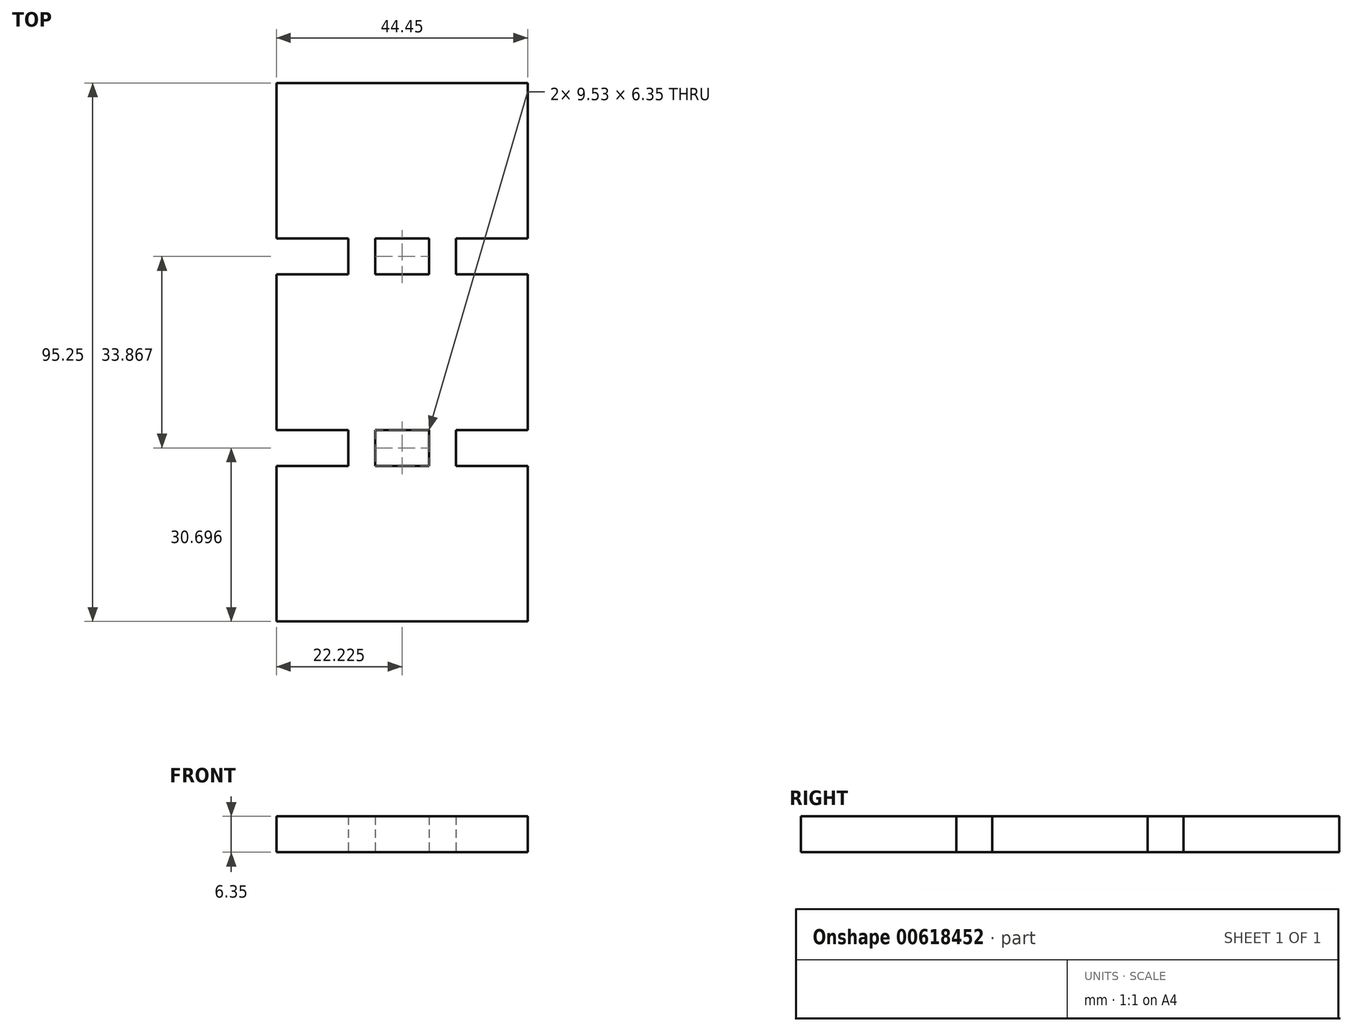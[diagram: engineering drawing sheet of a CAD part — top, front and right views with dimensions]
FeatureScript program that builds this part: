
annotation { "Feature Type Name" : "Feature", "Feature Type Description" : "" }
export const myFeature = defineFeature(function(context is Context, id is Id, definition is map)
    precondition{}
    {
        {
            var Q0;
            Q0=qCreatedBy(makeId("Top.planeOp"),FACE);
            var sketch = newSketch(context, id + "F0", { "sketchPlane" : qUnion([Q0])});
            skLineSegment(sketch, "E0.bottom", {"start": v(-25.4, -50.99) * mm, "end": v(19.05, -50.99) * mm});
            skLineSegment(sketch, "E0.top", {"start": v(-25.4, 44.26) * mm, "end": v(19.05, 44.26) * mm});
            skLineSegment(sketch, "E0.left", {"start": v(-25.4, -50.99) * mm, "end": v(-25.4, -23.47) * mm});
            skLineSegment(sketch, "E0.right", {"start": v(19.05, -50.99) * mm, "end": v(19.05, -23.47) * mm});
            skLineSegment(sketch, "E1.bottom", {"start": v(19.05, -17.12) * mm, "end": v(6.35, -17.12) * mm});
            skLineSegment(sketch, "E1.top", {"start": v(19.05, -23.47) * mm, "end": v(6.35, -23.47) * mm});
            skLineSegment(sketch, "E1.right", {"start": v(-12.7, -17.12) * mm, "end": v(-12.7, -23.47) * mm});
            skLineSegment(sketch, "E2.bottom", {"start": v(19.05, 16.75) * mm, "end": v(6.35, 16.75) * mm});
            skLineSegment(sketch, "E2.top", {"start": v(19.05, 10.4) * mm, "end": v(6.35, 10.4) * mm});
            skLineSegment(sketch, "E2.right", {"start": v(-12.7, 16.75) * mm, "end": v(-12.7, 10.4) * mm});
            skPoint(sketch, "E3.orphan", {"position": v(6.35, 16.75) * mm});
            skPoint(sketch, "E4.orphan", {"position": v(6.35, -23.47) * mm});
            skLineSegment(sketch, "E5.trimOffspring", {"start": v(19.05, 16.75) * mm, "end": v(19.05, 44.26) * mm});
            skLineSegment(sketch, "E6.trimOffspring", {"start": v(-25.4, 16.75) * mm, "end": v(-25.4, 44.26) * mm});
            skLineSegment(sketch, "E7.trimOffspring", {"start": v(19.05, -17.12) * mm, "end": v(19.05, 10.4) * mm});
            skLineSegment(sketch, "E8.trimOffspring", {"start": v(-25.4, -17.12) * mm, "end": v(-25.4, 10.4) * mm});
            skPoint(sketch, "E2.left.end.orphan", {"position": v(6.35, 10.4) * mm});
            skLineSegment(sketch, "E9", {"start": v(6.35, 16.75) * mm, "end": v(6.35, 10.4) * mm});
            skLineSegment(sketch, "E10.trimOffspring", {"start": v(-12.7, 16.75) * mm, "end": v(-25.4, 16.75) * mm});
            skLineSegment(sketch, "E11.trimOffspring", {"start": v(-12.7, 10.4) * mm, "end": v(-25.4, 10.4) * mm});
            skLineSegment(sketch, "E12.trimOffspring", {"start": v(-12.7, -17.12) * mm, "end": v(-25.4, -17.12) * mm});
            skLineSegment(sketch, "E13.trimOffspring", {"start": v(-12.7, -23.47) * mm, "end": v(-25.4, -23.47) * mm});
            skLineSegment(sketch, "E14", {"start": v(6.35, -17.12) * mm, "end": v(6.35, -23.47) * mm});
            skLineSegment(sketch, "E15.bottom", {"start": v(-7.94, -17.12) * mm, "end": v(1.59, -17.12) * mm});
            skLineSegment(sketch, "E15.top", {"start": v(-7.94, -23.47) * mm, "end": v(1.59, -23.47) * mm});
            skLineSegment(sketch, "E15.left", {"start": v(-7.94, -17.12) * mm, "end": v(-7.94, -23.47) * mm});
            skLineSegment(sketch, "E15.right", {"start": v(1.59, -17.12) * mm, "end": v(1.59, -23.47) * mm});
            skLineSegment(sketch, "E16", {"start": v(-25.4, -3.36) * mm, "end": v(19.05, -3.36) * mm, "construction": true});
            skLineSegment(sketch, "E17.MirrorCS", {"start": v(-7.94, 16.75) * mm, "end": v(1.59, 16.75) * mm});
            skLineSegment(sketch, "E18.MirrorCS", {"start": v(-7.94, 10.4) * mm, "end": v(1.59, 10.4) * mm});
            skLineSegment(sketch, "E19.MirrorCS", {"start": v(-7.94, 10.4) * mm, "end": v(-7.94, 16.75) * mm});
            skLineSegment(sketch, "E20.MirrorCS", {"start": v(1.59, 10.4) * mm, "end": v(1.59, 16.75) * mm});
            skSolve(sketch);
        }
        {
            var Q0;
            Q0=qSketchRegion(id+"F0",true);
            extrude(context, id + "F1", {"entities" : qUnion([Q0]), "depth" : 6.35 * mm, "offsetDistance" : 25.4 * mm});
        }
    });
